# Revit family: PRD_AR_SntryFttngsndccssrs_CModule_ACEX90201
name_source: partatom
category: Specialty Equipment
units: mm (PartAtom-declared; Revit-internal decimal feet)

## family parameters
Always vertical = Yes
Cut with Voids When Loaded = No
Enable Cutting in Views = No
Maintain Annotation Orientation = No
OmniClass Number = 23.65.05.11.11
OmniClass Title = Water Supply Systems
Part Type = Normal
Room Calculation Point = No
Round Connector Dimension = Use Diameter
Shared = No
Work Plane-Based = No

## types (1)
- ACEX9020
    AssetType = Fixed
    BIMObjectName = PRD_AR_SanitaryFittingsAndAccessories_CModule_ACEX9020
    BodyMaterial = PRD_AR_Plastic_White
    Category = Pr_40_20, Sanitary fittings and accessories
    Default Elevation = 0 mm  [stored 0 ft]
    Description = C module for compatible KWC electronic fittings for radio-controlled parameterization, read-out of statistical data, realisation of predefined calendar functions as well as grouping of fittings to perform predefined control functions via necessary app.
    Export Type to IFC As = IfcSanitaryTerminalType
    Features = Compatible KWC electronic fittings for radio-controlled parameterization.
    IfcExportAs = IfcSanitaryTerminalType
    IfcExportType = USERDEFINED
    Manufacturer = KWC Group Management AG
    ManufacturerName = KWC Group Management AG
    ManufacturerURL = www.kwc-professional.com
    Model = ACEX9020
    ModelNumber = 3600001331
    ModelReference = ACEX9020
    Name = C module ACEX9020
    NominalDepth = 0 mm  [stored 0 ft]
    NominalHeight = 0 mm  [stored 0 ft]
    NominalLength = 0 mm  [stored 0 ft]
    NominalWidth = 0 mm  [stored 0 ft]
    ProductInformation = http://pim.kwc.com
    Quantity = 1
    QuantityUom = piece
    Status = New
    Type IFC Predefined Type = USERDEFINED
    URL = www.kwc-professional.com
    Uniclass2015Code = Pr_40_20
    Uniclass2015Title = Sanitary fittings and accessories
    Uniclass2015Version = Products v1.36
    Version = 1

note: [stored X ft] marks values corroborated as IEEE doubles in the binary element streams (Revit-internal decimal feet)

## geometry (parser evidence)
native form markers: Sweep x5
no freeform markers — native parametric forms only
